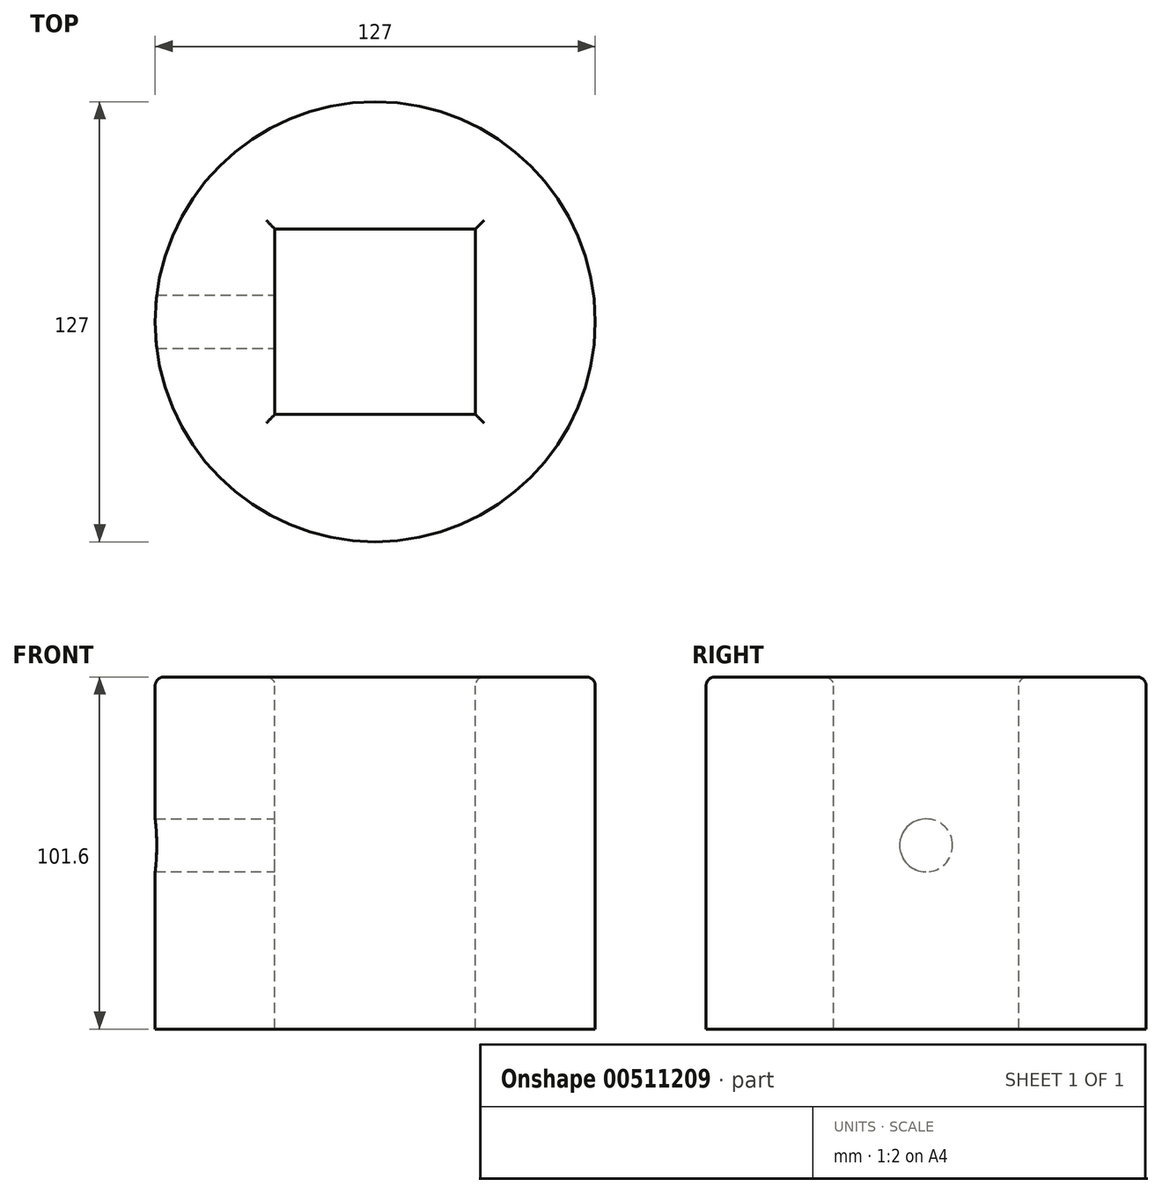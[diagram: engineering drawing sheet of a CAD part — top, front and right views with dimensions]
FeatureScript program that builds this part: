
annotation { "Feature Type Name" : "Feature", "Feature Type Description" : "" }
export const myFeature = defineFeature(function(context is Context, id is Id, definition is map)
    precondition{}
    {
        {
            var Q0;
            Q0=qCreatedBy(makeId("Top.planeOp"),FACE);
            var sketch = newSketch(context, id + "F0", { "sketchPlane" : qUnion([Q0])});
            skCircle(sketch, "E0", {"center": v(0, 0) * mm, "radius": 63.5 * mm});
            skSolve(sketch);
        }
        {
            var Q0;
            Q0=makeQuery(id+"F0.imprint","IMPRINT",FACE,{"disambiguationData":[TD([[makeQuery(id+"F0.imprint","IMPRINT",EDGE,{"derivedFrom":sQuery(id+"F0.wireOp",EDGE,"E0")}),1.0]])]});
            extrude(context, id + "F1", {"entities" : qUnion([Q0]), "depth" : 101.6 * mm});
        }
        {
            var Q0;
            Q0=makeQuery(id+"F1.opExtrude","CAP_FACE",FACE,{"disambiguationData":[OSD([sQuery(id+"F0.wireOp",EDGE,"E0")])],"isStart":false});
            var sketch = newSketch(context, id + "F2", { "sketchPlane" : qUnion([Q0])});
            skLineSegment(sketch, "E1.bottom", {"start": v(28.92, -26.73) * mm, "end": v(-28.92, -26.73) * mm});
            skLineSegment(sketch, "E1.top", {"start": v(28.92, 26.73) * mm, "end": v(-28.92, 26.73) * mm});
            skLineSegment(sketch, "E1.left", {"start": v(28.92, -26.73) * mm, "end": v(28.92, 26.73) * mm});
            skLineSegment(sketch, "E1.right", {"start": v(-28.92, -26.73) * mm, "end": v(-28.92, 26.73) * mm});
            skPoint(sketch, "E1.middle", {"position": v(0, 0) * mm});
            skSolve(sketch);
        }
        {
            var Q0;
            Q0=makeQuery(id+"F2.imprint","IMPRINT",FACE,{"disambiguationData":[TD([[makeQuery(id+"F2.imprint","IMPRINT",EDGE,{"derivedFrom":sQuery(id+"F2.wireOp",EDGE,"E1.bottom")}),-1.0]])]});
            extrude(context, id + "F3", {"entities" : qUnion([Q0]), "operationType" : NewBodyOperationType.REMOVE, "oppositeDirection" : true, "depth" : 190.5 * mm});
        }
        {
            var Q0;
            Q0=makeQuery(id+"F1.opExtrude","CAP_FACE",FACE,{"disambiguationData":[OSD([sQuery(id+"F0.wireOp",EDGE,"E0")])],"isStart":false});
            fillet(context, id + "F4", {"entities" : qUnion([Q0]), "radius" : 2.54 * mm, "tangentPropagation" : true, "allowEdgeOverflow" : false});
        }
        {
            var Q0;
            Q0=makeQuery(id+"F3.boolean.opBoolean","COPY",FACE,{"derivedFrom":makeQuery(id+"F3.opExtrude","SWEPT_FACE",FACE,{"disambiguationData":[OSD([sQuery(id+"F2.wireOp",EDGE,"E1.right")])]})});
            var sketch = newSketch(context, id + "F5", { "sketchPlane" : qUnion([Q0])});
            skCircle(sketch, "E2", {"center": v(0, 53) * mm, "radius": 7.63 * mm});
            skSolve(sketch);
        }
        {
            var Q0;
            Q0=makeQuery(id+"F5.imprint","IMPRINT",FACE,{"disambiguationData":[TD([[makeQuery(id+"F5.imprint","IMPRINT",EDGE,{"derivedFrom":sQuery(id+"F5.wireOp",EDGE,"E2")}),1.0]])]});
            var Q1;
            Q1=sQuery(id+"F5.wireOp",EDGE,"E2");
            extrude(context, id + "F6", {"entities" : qUnion([Q0]), "operationType" : NewBodyOperationType.REMOVE, "surfaceEntities" : qUnion([Q1]), "oppositeDirection" : true, "depth" : 57.9 * mm});
        }
    });
